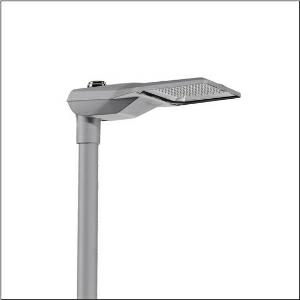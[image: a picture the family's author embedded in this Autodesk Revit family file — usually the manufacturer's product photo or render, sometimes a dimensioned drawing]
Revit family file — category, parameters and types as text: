
# Revit family: streetlight_sl_21_midi___st1_5a_5xe7p47n08lb_54ff
name_source: partatom
category: Lighting Fixtures
units: mm (PartAtom-declared; Revit-internal decimal feet)

## family parameters
Cut with Voids When Loaded = No
Host = Face
Light Source = No
Part Type = Normal
Room Calculation Point = No
Round Connector Dimension = Use Diameter
Shared = No

## types (1)
- --- (1 x LED, 14690 lm, 98.3 W, 4000K)
    Apparent Load = 98 VA
    CIE Flux Codes = 22 53 95 100 100
    Color Rendering = 70
    Color Temperature = 4000K
    Default Elevation = 1800 mm
    Description = Streetlight SL 21 midi, mast luminaire, primary light control with lens, of PMMA, primary optical cover: cover, of toughened safety glass, transparent, light distribution: ST1.5a, light emission: direct distribution, primary light characteristic: asymmetric, installation type: side-entry, LED, 3G 2.5mm², High Power LED, rated luminous flux: 14.690lm, luminous efficacy: 149lm/W, light colour: 740, colour temperature: 4000K, control gear: NEMA (7pin), control: overheat protection, pre-setting: linear dimming characteristic, constant luminous flux control, time-dependent luminous flux control, flexible luminous flux parameterisation, mains connection: 220..240V, AC, 50/60Hz, connection cable pre-assembled, cable length: 10,5m, wiring characteristics: H05VV-F, start of lifetime: 98W, end of service life: 101W, reduction: 45W, luminaire housing, of diecast aluminium (EN AC-44300), powder-coated, SITECO metallic grey (DB 702S), corrosivity category C5 high according to DIN EN ISO 12944, multi-level sealing system, sealing non-destructively replaceable, inclination adjustable: 0°, 5°, 10°, 15°, length: 644mm, width: 335mm, height: 110mm, spigot size: 42mm (side-entry), mounting height: 4..8m, protection rating (complete): IP66, insulation class (complete): insulation class I (protective earthing), certification: CE, ENEC, ENEC+, VDE, impact resistance: IK10, permissible operating ambient temperature for outdoor applications: -40..+50°C, standard-compliant lighting for roads and squares, packaging unit: 1 piece

Light Distribution: ST1.5a
    Height = 111 mm
    Lamp = 1 x LED
    Lamp Light Flux = 14690 lm
    Lamp Power = 98.3 W
    Lamp count = 1
    Length = 644 mm
    Luminous efficacy = 149 lm/W
    Manufacturer = Siteco
    ModVariant = No
    Model = 5XE7P47N08LB
    Number of Poles = 1
    OnlyDefault = Yes
    Power Factor = 1
    Product Name = Streetlight SL 21 midi | ST1.5a
    Product group = mast luminaire | pylon top
    ProductGroupID = 6100
    Protection Class = Protection class I
    Protection Degree = IP 66
    RLX_Detail_Level = 1
    RLX_Emergency_Light_Flux = 0 lm
    RLX_Emergency_Type = 0
    RLX_Emergency_Type_DB = No
    RlxData = <blob elided: 30225 chars, md5=27e6474d>
    Socket = socket
    Standby Power = 0 W
    System Light Flux = 14690 lm
    System Power = 98 W
    Type Comments = factory setting: luminous flux: 100 % | dim-lin: 254 | 1020 mA
    Type Image = l_1294377.jpg
    URL = http://relux.com
    VarID = @adj_132917
    Voltage = 0 V
    Weight = 0.00 kg
    Width = 336 mm

## geometry (parser evidence)
native form markers: Blend x4, Sweep x7
no freeform markers — native parametric forms only
